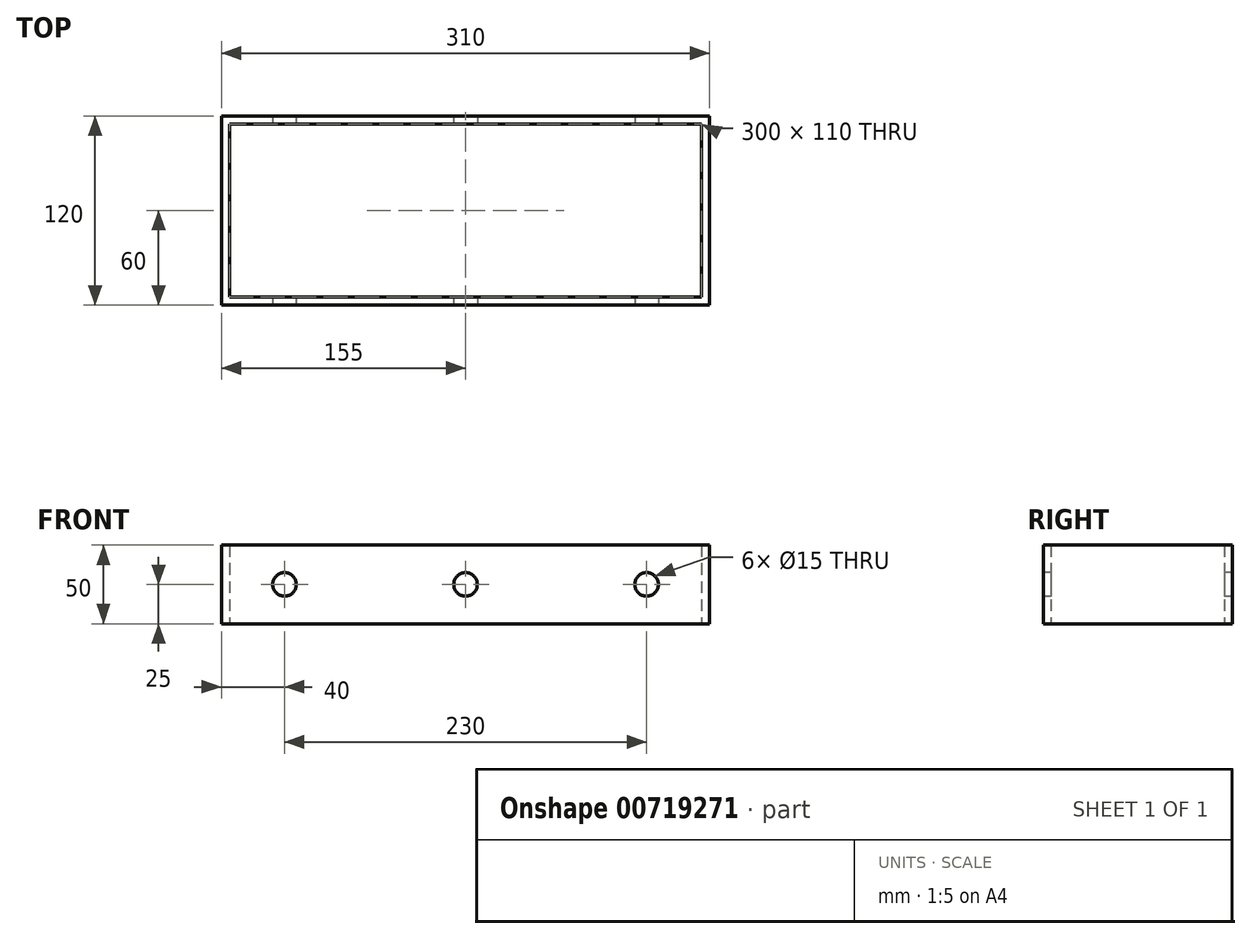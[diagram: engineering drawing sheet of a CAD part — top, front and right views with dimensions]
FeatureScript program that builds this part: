
annotation { "Feature Type Name" : "Feature", "Feature Type Description" : "" }
export const myFeature = defineFeature(function(context is Context, id is Id, definition is map)
    precondition{}
    {
        {
            var Q0;
            Q0=qCreatedBy(makeId("Top.planeOp"),FACE);
            var sketch = newSketch(context, id + "F0", { "sketchPlane" : qUnion([Q0])});
            skLineSegment(sketch, "E0.bottom", {"start": v(-155, 60) * mm, "end": v(155, 60) * mm});
            skLineSegment(sketch, "E0.top", {"start": v(-155, -60) * mm, "end": v(155, -60) * mm});
            skLineSegment(sketch, "E0.left", {"start": v(-155, 60) * mm, "end": v(-155, -60) * mm});
            skLineSegment(sketch, "E0.right", {"start": v(155, 60) * mm, "end": v(155, -60) * mm});
            skPoint(sketch, "E0.middle", {"position": v(0, 0) * mm});
            skLineSegment(sketch, "E1.bottom", {"start": v(-150, 55) * mm, "end": v(150, 55) * mm});
            skLineSegment(sketch, "E1.top", {"start": v(-150, -55) * mm, "end": v(150, -55) * mm});
            skLineSegment(sketch, "E1.left", {"start": v(-150, 55) * mm, "end": v(-150, -55) * mm});
            skLineSegment(sketch, "E1.right", {"start": v(150, 55) * mm, "end": v(150, -55) * mm});
            skSolve(sketch);
        }
        {
            var Q0;
            Q0=makeQuery(id+"F0.imprint","IMPRINT",FACE,{"disambiguationData":[TD([[makeQuery(id+"F0.imprint","IMPRINT",EDGE,{"derivedFrom":sQuery(id+"F0.wireOp",EDGE,"E0.bottom")}),-1.0]])]});
            extrude(context, id + "F1", {"entities" : qUnion([Q0]), "depth" : 50 * mm, "offsetDistance" : 25 * mm});
        }
        {
            var Q0;
            Q0=makeQuery(id+"F1.opExtrude","SWEPT_FACE",FACE,{"disambiguationData":[OSD([sQuery(id+"F0.wireOp",EDGE,"E0.top")])]});
            var sketch = newSketch(context, id + "F2", { "sketchPlane" : qUnion([Q0])});
            skCircle(sketch, "E2", {"center": v(-115, 25) * mm, "radius": 7.5 * mm});
            skCircle(sketch, "E3", {"center": v(0, 25) * mm, "radius": 7.5 * mm});
            skCircle(sketch, "E4", {"center": v(115, 25) * mm, "radius": 7.5 * mm});
            skSolve(sketch);
        }
        {
            var Q0;
            Q0=makeQuery(id+"F2.imprint","IMPRINT",FACE,{"disambiguationData":[TD([[makeQuery(id+"F2.imprint","IMPRINT",EDGE,{"derivedFrom":sQuery(id+"F2.wireOp",EDGE,"E2")}),1.0]])]});
            var Q1;
            Q1=makeQuery(id+"F2.imprint","IMPRINT",FACE,{"disambiguationData":[TD([[makeQuery(id+"F2.imprint","IMPRINT",EDGE,{"derivedFrom":sQuery(id+"F2.wireOp",EDGE,"E3")}),1.0]])]});
            var Q2;
            Q2=makeQuery(id+"F2.imprint","IMPRINT",FACE,{"disambiguationData":[TD([[makeQuery(id+"F2.imprint","IMPRINT",EDGE,{"derivedFrom":sQuery(id+"F2.wireOp",EDGE,"E4")}),1.0]])]});
            extrude(context, id + "F3", {"entities" : qUnion([Q0, Q1, Q2]), "operationType" : NewBodyOperationType.REMOVE, "oppositeDirection" : true, "depth" : 150 * mm, "offsetDistance" : 25 * mm});
        }
    });
